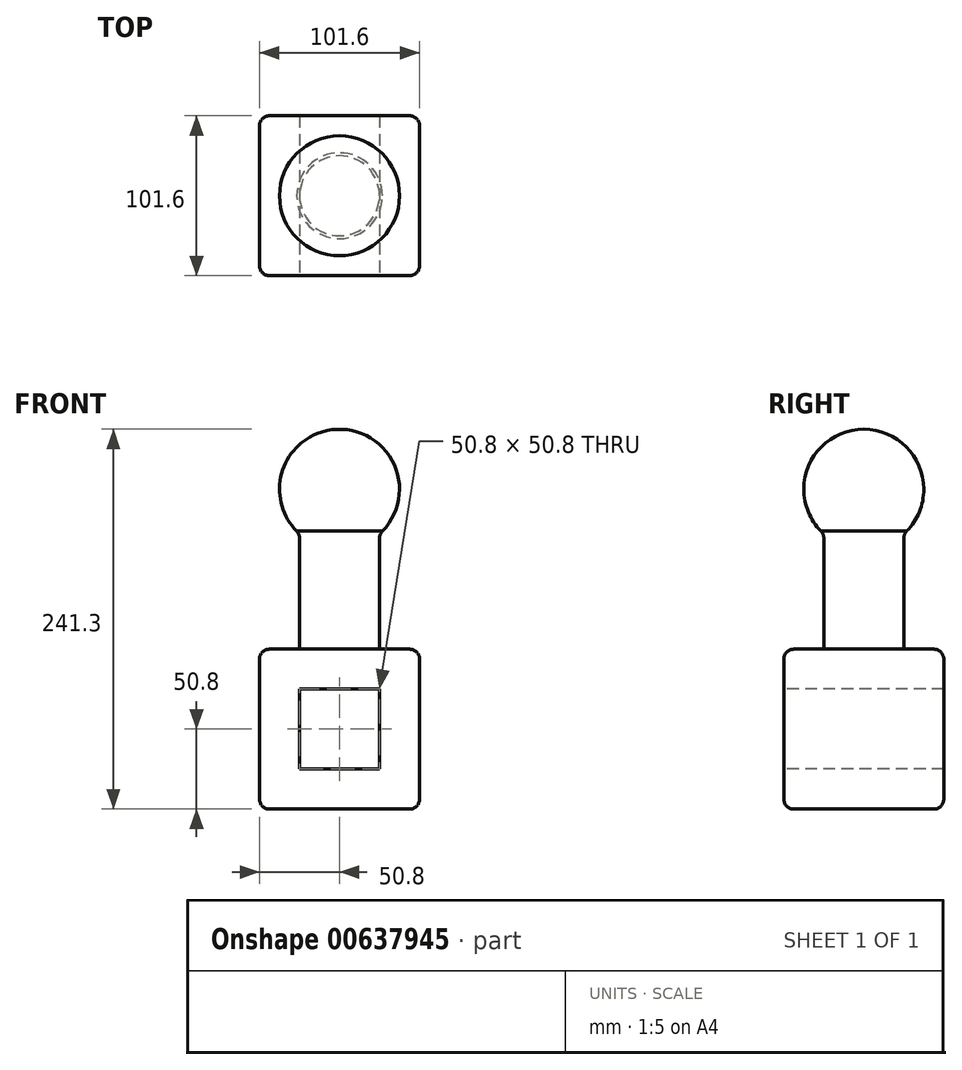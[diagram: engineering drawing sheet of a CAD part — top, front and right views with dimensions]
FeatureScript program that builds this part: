
annotation { "Feature Type Name" : "Feature", "Feature Type Description" : "" }
export const myFeature = defineFeature(function(context is Context, id is Id, definition is map)
    precondition{}
    {
        {
            var Q0;
            Q0=qCreatedBy(makeId("Top.planeOp"),FACE);
            var sketch = newSketch(context, id + "F0", { "sketchPlane" : qUnion([Q0])});
            skLineSegment(sketch, "E0.bottom", {"start": v(50.8, 50.8) * mm, "end": v(-50.8, 50.8) * mm});
            skLineSegment(sketch, "E0.top", {"start": v(50.8, -50.8) * mm, "end": v(-50.8, -50.8) * mm});
            skLineSegment(sketch, "E0.left", {"start": v(50.8, 50.8) * mm, "end": v(50.8, -50.8) * mm});
            skLineSegment(sketch, "E0.right", {"start": v(-50.8, 50.8) * mm, "end": v(-50.8, -50.8) * mm});
            skPoint(sketch, "E0.middle", {"position": v(0, 0) * mm});
            skSolve(sketch);
        }
        {
            var Q0;
            Q0=makeQuery(id+"F0.imprint","IMPRINT",FACE,{"disambiguationData":[TD([[makeQuery(id+"F0.imprint","IMPRINT",EDGE,{"derivedFrom":sQuery(id+"F0.wireOp",EDGE,"E0.bottom")}),1.0]])]});
            extrude(context, id + "F1", {"entities" : qUnion([Q0]), "depth" : 101.6 * mm, "offsetDistance" : 25.4 * mm});
        }
        {
            var Q0;
            Q0=makeQuery(id+"F1.opExtrude","CAP_FACE",FACE,{"disambiguationData":[OSD([sQuery(id+"F0.wireOp",EDGE,"E0.bottom"),sQuery(id+"F0.wireOp",EDGE,"E0.top"),sQuery(id+"F0.wireOp",EDGE,"E0.left"),sQuery(id+"F0.wireOp",EDGE,"E0.right")])],"isStart":false});
            var sketch = newSketch(context, id + "F2", { "sketchPlane" : qUnion([Q0])});
            skCircle(sketch, "E1", {"center": v(0, 0) * mm, "radius": 25.4 * mm});
            skSolve(sketch);
        }
        {
            var Q0;
            Q0=makeQuery(id+"F2.imprint","IMPRINT",FACE,{"disambiguationData":[TD([[makeQuery(id+"F2.imprint","IMPRINT",EDGE,{"derivedFrom":sQuery(id+"F2.wireOp",EDGE,"E1")}),1.0]])]});
            extrude(context, id + "F3", {"entities" : qUnion([Q0]), "operationType" : NewBodyOperationType.ADD, "depth" : 101.6 * mm, "offsetDistance" : 25.4 * mm});
        }
        {
            var Q0;
            Q0=makeQuery(id+"F3.opExtrude","CAP_FACE",FACE,{"disambiguationData":[OSD([sQuery(id+"F2.wireOp",EDGE,"E1")])],"isStart":false});
            var sketch = newSketch(context, id + "F4", { "sketchPlane" : qUnion([Q0])});
            skArc(sketch, "E2", {"start": v(0, -38.1) * mm, "mid": v(38.1, 0) * mm, "end": v(0, 38.1) * mm});
            skLineSegment(sketch, "E3", {"start": v(0, 38.1) * mm, "end": v(0, -38.1) * mm});
            skSolve(sketch);
        }
        {
            var Q0;
            {var subQ0=sQuery(id+"F4.wireOp",EDGE,"E3");var subQ1=makeQuery(id+"F3.opExtrude","CAP_EDGE",EDGE,{"disambiguationData":[OSD([sQuery(id+"F2.wireOp",EDGE,"E1")])],"isStart":false});var subQ2=makeQuery(id+"F4.imprint","INTERSECT",VERTEX,{"disambiguationData":[OD(0.0)],"derivedFrom":[subQ1,subQ0]});Q0=makeQuery(id+"F4.imprint","IMPRINT",FACE,{"disambiguationData":[TD([[makeQuery(id+"F4.imprint","IMPRINT",EDGE,{"disambiguationData":[TD([[subQ2,-1.0]])],"derivedFrom":subQ0}),1.0]])]});}
            var Q1;
            {var subQ0=sQuery(id+"F4.wireOp",EDGE,"E2");Q1=makeQuery(id+"F4.imprint","IMPRINT",FACE,{"disambiguationData":[TD([[makeQuery(id+"F4.imprint","IMPRINT",EDGE,{"derivedFrom":subQ0}),1.0]])]});}
            var Q2;
            Q2=sQuery(id+"F4.wireOp",EDGE,"E3");
            revolve(context, id + "F5", {"operationType" : NewBodyOperationType.ADD, "entities" : qUnion([Q0, Q1]), "axis" : qUnion([Q2]), "revolveType" : RevolveType.FULL});
        }
        {
            var Q0;
            Q0=makeQuery(id+"F1.opExtrude","SWEPT_FACE",FACE,{"disambiguationData":[OSD([sQuery(id+"F0.wireOp",EDGE,"E0.top")])]});
            var sketch = newSketch(context, id + "F6", { "sketchPlane" : qUnion([Q0])});
            skLineSegment(sketch, "E4.bottom", {"start": v(25.4, 76.2) * mm, "end": v(-25.4, 76.2) * mm});
            skLineSegment(sketch, "E4.top", {"start": v(25.4, 25.4) * mm, "end": v(-25.4, 25.4) * mm});
            skLineSegment(sketch, "E4.left", {"start": v(25.4, 76.2) * mm, "end": v(25.4, 25.4) * mm});
            skLineSegment(sketch, "E4.right", {"start": v(-25.4, 76.2) * mm, "end": v(-25.4, 25.4) * mm});
            skPoint(sketch, "E4.middle", {"position": v(0, 50.8) * mm});
            skPoint(sketch, "E4.middle.positionSnap0", {"position": v(50.8, 50.8) * mm});
            skPoint(sketch, "E4.centerSnap0", {"position": v(50.8, 50.8) * mm});
            skSolve(sketch);
        }
        {
            var Q0;
            Q0=makeQuery(id+"F6.imprint","IMPRINT",FACE,{"disambiguationData":[TD([[makeQuery(id+"F6.imprint","IMPRINT",EDGE,{"derivedFrom":sQuery(id+"F6.wireOp",EDGE,"E4.bottom")}),1.0]])]});
            extrude(context, id + "F7", {"entities" : qUnion([Q0]), "operationType" : NewBodyOperationType.REMOVE, "oppositeDirection" : true, "depth" : 101.6 * mm, "offsetDistance" : 25.4 * mm});
        }
        {
            var Q0;
            Q0=makeQuery(id+"F1.opExtrude","CAP_EDGE",EDGE,{"disambiguationData":[OSD([sQuery(id+"F0.wireOp",EDGE,"E0.bottom")])],"isStart":false});
            var Q1;
            Q1=makeQuery(id+"F1.opExtrude","CAP_EDGE",EDGE,{"disambiguationData":[OSD([sQuery(id+"F0.wireOp",EDGE,"E0.right")])],"isStart":false});
            var Q2;
            Q2=makeQuery(id+"F1.opExtrude","CAP_EDGE",EDGE,{"disambiguationData":[OSD([sQuery(id+"F0.wireOp",EDGE,"E0.top")])],"isStart":false});
            var Q3;
            Q3=makeQuery(id+"F1.opExtrude","CAP_EDGE",EDGE,{"disambiguationData":[OSD([sQuery(id+"F0.wireOp",EDGE,"E0.left")])],"isStart":false});
            var Q4;
            Q4=makeQuery(id+"F3.opExtrude","CAP_EDGE",EDGE,{"disambiguationData":[OSD([sQuery(id+"F2.wireOp",EDGE,"E1")])],"isStart":true});
            var Q5;
            Q5=makeQuery(id+"F1.opExtrude","SWEPT_EDGE",EDGE,{"disambiguationData":[OSD([sQuery(id+"F0.wireOp",EDGE,"E0.top"),sQuery(id+"F0.wireOp",EDGE,"E0.right")])]});
            var Q6;
            Q6=makeQuery(id+"F1.opExtrude","SWEPT_EDGE",EDGE,{"disambiguationData":[OSD([sQuery(id+"F0.wireOp",EDGE,"E0.bottom"),sQuery(id+"F0.wireOp",EDGE,"E0.right")])]});
            var Q7;
            Q7=makeQuery(id+"F1.opExtrude","CAP_EDGE",EDGE,{"disambiguationData":[OSD([sQuery(id+"F0.wireOp",EDGE,"E0.right")])],"isStart":true});
            var Q8;
            Q8=makeQuery(id+"F1.opExtrude","CAP_EDGE",EDGE,{"disambiguationData":[OSD([sQuery(id+"F0.wireOp",EDGE,"E0.top")])],"isStart":true});
            var Q9;
            Q9=makeQuery(id+"F1.opExtrude","SWEPT_EDGE",EDGE,{"disambiguationData":[OSD([sQuery(id+"F0.wireOp",EDGE,"E0.top"),sQuery(id+"F0.wireOp",EDGE,"E0.left")])]});
            var Q10;
            Q10=makeQuery(id+"F1.opExtrude","SWEPT_EDGE",EDGE,{"disambiguationData":[OSD([sQuery(id+"F0.wireOp",EDGE,"E0.bottom"),sQuery(id+"F0.wireOp",EDGE,"E0.left")])]});
            var Q11;
            Q11=makeQuery(id+"F1.opExtrude","CAP_EDGE",EDGE,{"disambiguationData":[OSD([sQuery(id+"F0.wireOp",EDGE,"E0.bottom")])],"isStart":true});
            var Q12;
            Q12=makeQuery(id+"F1.opExtrude","CAP_EDGE",EDGE,{"disambiguationData":[OSD([sQuery(id+"F0.wireOp",EDGE,"E0.left")])],"isStart":true});
            fillet(context, id + "F8", {"entities" : qUnion([Q0, Q1, Q2, Q3, Q4, Q5, Q6, Q7, Q8, Q9, Q10, Q11, Q12]), "radius" : 6.35 * mm, "tangentPropagation" : true, "allowEdgeOverflow" : false});
        }
        {
            var Q0;
            Q0=makeQuery(id+"F5.boolean.opBoolean","INTERSECT",EDGE,{"derivedFrom":[makeQuery(id+"F3.opExtrude","SWEPT_FACE",FACE,{"disambiguationData":[OSD([sQuery(id+"F2.wireOp",EDGE,"E1")])]}),makeQuery(id+"F5.opRevolve","SWEPT_FACE",FACE,{"disambiguationData":[OSD([sQuery(id+"F4.wireOp",EDGE,"E2")])]})]});
            fillet(context, id + "F9", {"entities" : qUnion([Q0]), "radius" : 6.35 * mm, "tangentPropagation" : true, "allowEdgeOverflow" : false});
        }
    });
